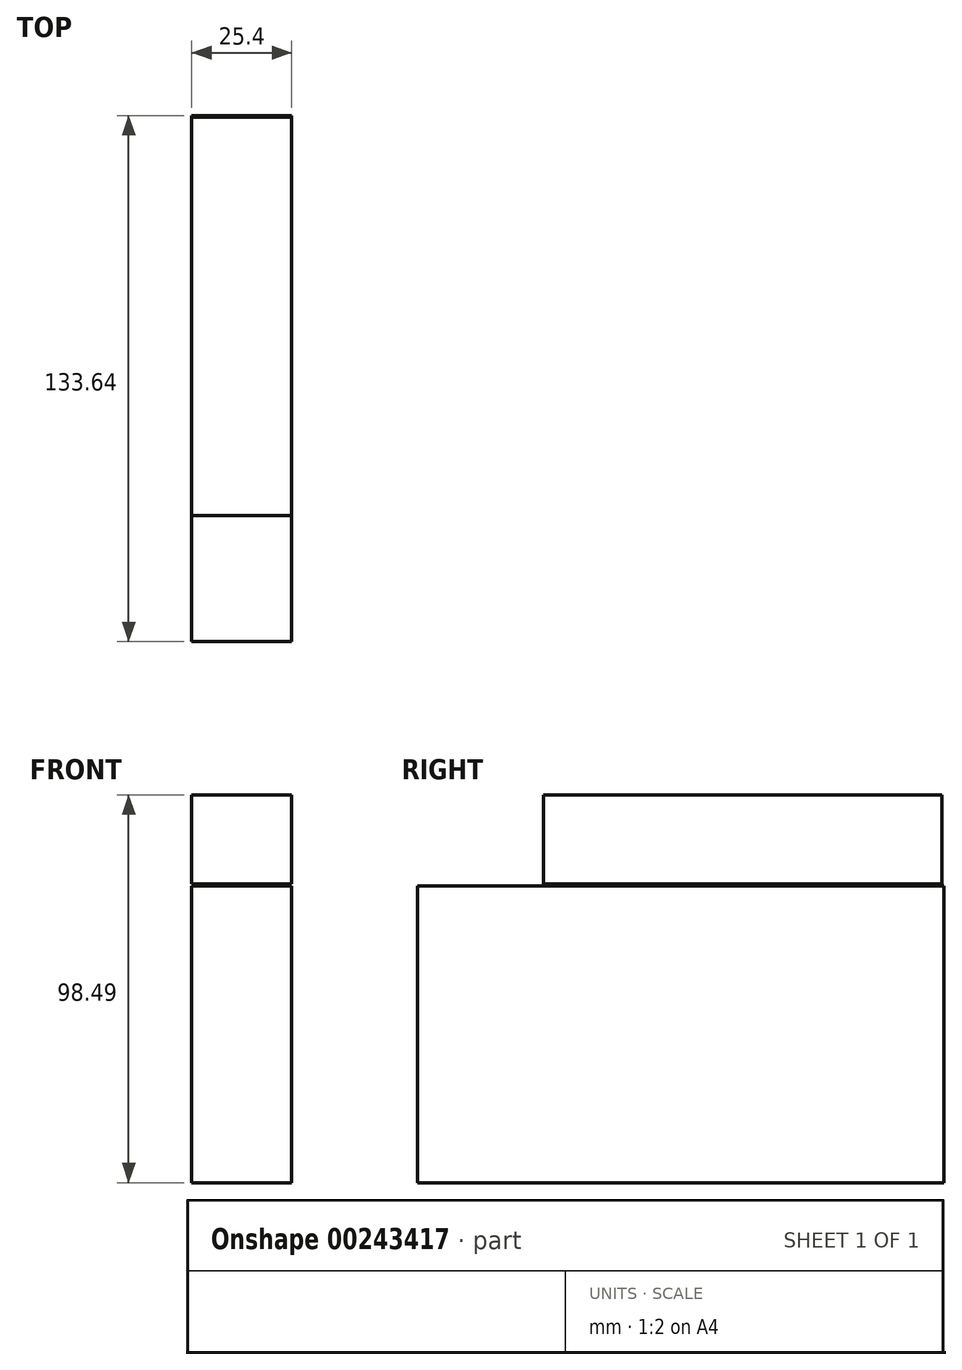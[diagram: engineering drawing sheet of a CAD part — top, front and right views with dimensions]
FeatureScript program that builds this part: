
annotation { "Feature Type Name" : "Feature", "Feature Type Description" : "" }
export const myFeature = defineFeature(function(context is Context, id is Id, definition is map)
    precondition{}
    {
        {
            var Q0;
            Q0=qCreatedBy(makeId("Right.planeOp"),FACE);
            var sketch = newSketch(context, id + "F0", { "sketchPlane" : qUnion([Q0])});
            skLineSegment(sketch, "E0.bottom", {"start": v(-66.82, 37.7) * mm, "end": v(66.82, 37.7) * mm});
            skLineSegment(sketch, "E0.top", {"start": v(-66.82, -37.7) * mm, "end": v(66.82, -37.7) * mm});
            skLineSegment(sketch, "E0.left", {"start": v(-66.82, 37.7) * mm, "end": v(-66.82, -37.7) * mm});
            skLineSegment(sketch, "E0.right", {"start": v(66.82, 37.7) * mm, "end": v(66.82, -37.7) * mm});
            skPoint(sketch, "E0.middle", {"position": v(0, 0) * mm});
            skSolve(sketch);
        }
        {
            var Q0;
            Q0=makeQuery(id+"F0.imprint","IMPRINT",FACE,{"disambiguationData":[TD([[makeQuery(id+"F0.imprint","IMPRINT",EDGE,{"derivedFrom":sQuery(id+"F0.wireOp",EDGE,"E0.bottom")}),-1.0]])]});
            extrude(context, id + "F1", {"entities" : qUnion([Q0]), "depth" : 25.4 * mm});
        }
        {
            var Q0;
            Q0=qCreatedBy(makeId("Right.planeOp"),FACE);
            var sketch = newSketch(context, id + "F2", { "sketchPlane" : qUnion([Q0])});
            skLineSegment(sketch, "E1.bottom", {"start": v(66.37, 38.15) * mm, "end": v(0, 38.15) * mm});
            skLineSegment(sketch, "E1.top", {"start": v(66.37, 60.8) * mm, "end": v(0, 60.8) * mm});
            skLineSegment(sketch, "E1.left", {"start": v(66.37, 38.15) * mm, "end": v(66.37, 60.8) * mm});
            skLineSegment(sketch, "E1.right", {"start": v(0, 38.15) * mm, "end": v(0, 60.8) * mm});
            skSolve(sketch);
        }
        {
            var Q0;
            Q0=makeQuery(id+"F2.imprint","IMPRINT",FACE,{"disambiguationData":[TD([[makeQuery(id+"F2.imprint","IMPRINT",EDGE,{"derivedFrom":sQuery(id+"F2.wireOp",EDGE,"E1.bottom")}),-1.0]])]});
            extrude(context, id + "F3", {"entities" : qUnion([Q0]), "depth" : 25.4 * mm});
        }
        {
            var Q0;
            Q0=makeQuery(id+"F3.opExtrude","SWEPT_FACE",FACE,{"disambiguationData":[OSD([sQuery(id+"F2.wireOp",EDGE,"E1.right")])]});
            extrude(context, id + "F4", {"entities" : qUnion([Q0]), "operationType" : NewBodyOperationType.ADD, "depth" : 34.8 * mm});
        }
    });
